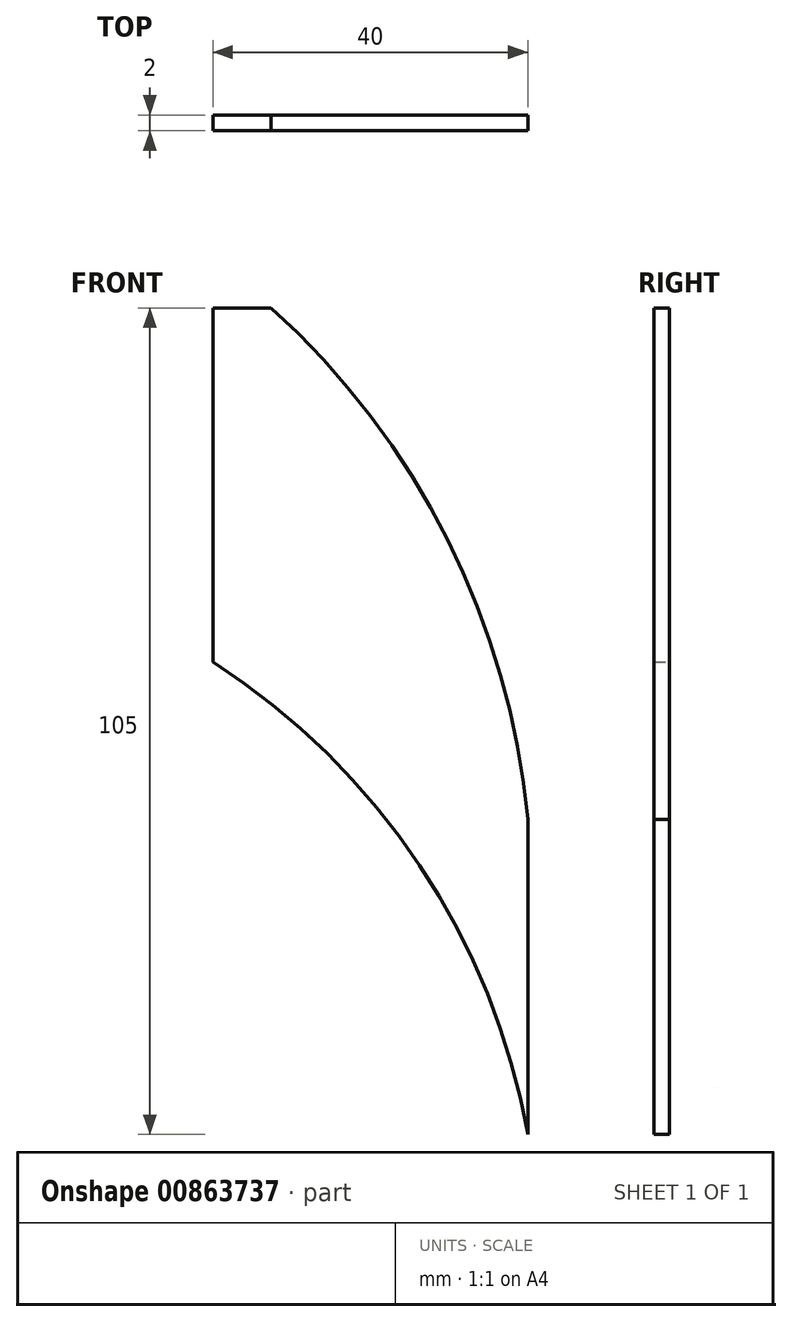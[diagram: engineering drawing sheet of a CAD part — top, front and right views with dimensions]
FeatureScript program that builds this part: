
annotation { "Feature Type Name" : "Feature", "Feature Type Description" : "" }
export const myFeature = defineFeature(function(context is Context, id is Id, definition is map)
    precondition{}
    {
        {
            var Q0;
            Q0=qCreatedBy(makeId("Front.planeOp"),FACE);
            var sketch = newSketch(context, id + "F0", { "sketchPlane" : qUnion([Q0])});
            skLineSegment(sketch, "E0", {"start": v(0, 0) * mm, "end": v(0, 45) * mm});
            skLineSegment(sketch, "E1", {"start": v(0, 45) * mm, "end": v(7.39, 45) * mm});
            skArc(sketch, "E2", {"start": v(40, -60) * mm, "mid": v(26.27, -25.82) * mm, "end": v(0, 0) * mm});
            skArc(sketch, "E3", {"start": v(40, -20) * mm, "mid": v(29.81, 15.57) * mm, "end": v(7.4, 45) * mm});
            skLineSegment(sketch, "E4", {"start": v(40, -60) * mm, "end": v(40, -20) * mm});
            skSolve(sketch);
        }
        {
            var Q0;
            Q0 = qSketchRegion(id + "F0", true);
            extrude(context, id + "F1", {"entities" : qUnion([Q0]), "depth" : 2 * mm, "offsetDistance" : 25 * mm});
        }
    });
